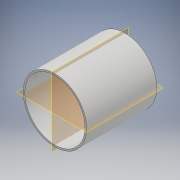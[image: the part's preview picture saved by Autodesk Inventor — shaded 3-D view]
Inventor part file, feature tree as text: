
AUTODESK INVENTOR PART (.ipt)
format: ipt  version: 2017 (Build 210142000, 142)  size: 102,400 bytes
history: native  units: mm
features: extrude x1, sketch x1
ambient origin geometry x8: Origin, YZ Plane, XZ Plane, XY Plane, X Axis, Y Axis, Z Axis, Center Point
bodies: Solid1 (feature_tree)
feature tree (2):
  extrude  "Extrusion1"  Depth=84.0mm
  sketch  "Sketch1"  dims[d0=76.0mm d1=2.0mm d2=84.0mm d3=0.0mm]
